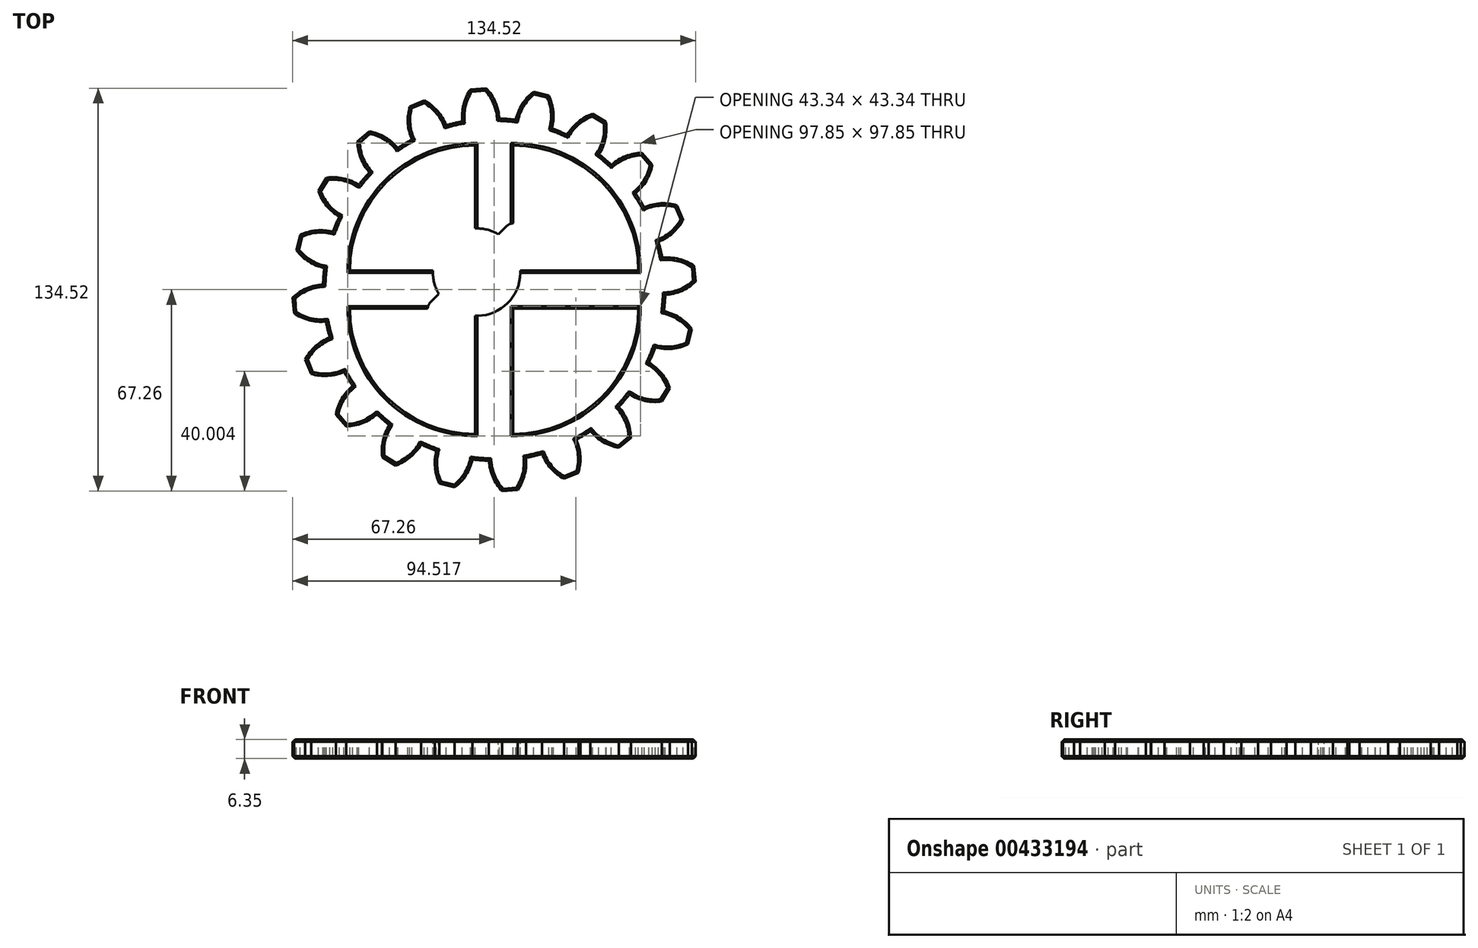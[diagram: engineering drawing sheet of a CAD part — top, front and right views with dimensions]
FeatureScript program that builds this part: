
annotation { "Feature Type Name" : "Feature", "Feature Type Description" : "" }
export const myFeature = defineFeature(function(context is Context, id is Id, definition is map)
    precondition{}
    {
        {
            var Q0;
            Q0=qCreatedBy(makeId("Top.planeOp"),FACE);
            var sketch = newSketch(context, id + "F0", { "sketchPlane" : qUnion([Q0])});
            skCircle(sketch, "E0", {"center": v(0, 0) * mm, "radius": 30.48 * mm, "construction": true});
            skSolve(sketch);
        }
        {
            var Q0;
            Q0=qCreatedBy(makeId("Top.planeOp"),FACE);
            var sketch = newSketch(context, id + "F1", { "sketchPlane" : qUnion([Q0])});
            skCircle(sketch, "E1", {"center": v(0, 0) * mm, "radius": 67.31 * mm, "construction": true});
            skCircle(sketch, "E2", {"center": v(0, 0) * mm, "radius": 63.5 * mm, "construction": true});
            skCircle(sketch, "E3", {"center": v(0, 0) * mm, "radius": 57.15 * mm, "construction": true});
            skLineSegment(sketch, "E4", {"start": v(0, 0) * mm, "end": v(0, 89.78) * mm, "construction": true});
            skLineSegment(sketch, "E5", {"start": v(0, 0) * mm, "end": v(-7.61, 96.72) * mm, "construction": true});
            skLineSegment(sketch, "E6", {"start": v(0, 63.5) * mm, "end": v(-65.71, 63.5) * mm, "construction": true});
            skLineSegment(sketch, "E7", {"start": v(0, 63.5) * mm, "end": v(-58.85, 37.3) * mm, "construction": true});
            skCircle(sketch, "E8", {"center": v(0, 63.5) * mm, "radius": 15.88 * mm, "construction": true});
            skCircle(sketch, "E9", {"center": v(0, 0) * mm, "radius": 58.01 * mm, "construction": true});
            skCircle(sketch, "E10", {"center": v(-14.13, 56.26) * mm, "radius": 15.88 * mm, "construction": true});
            skArc(sketch, "E11", {"start": v(1.72, 57.12) * mm, "mid": v(0.43, 62.59) * mm, "end": v(-2.68, 67.26) * mm});
            skArc(sketch, "E12.MirrorCS", {"start": v(-10.64, 56.15) * mm, "mid": v(-10.22, 61.75) * mm, "end": v(-7.88, 66.85) * mm});
            skLineSegment(sketch, "E13", {"start": v(-7.88, 66.85) * mm, "end": v(-2.68, 67.26) * mm});
            skArc(sketch, "E14", {"start": v(-10.64, 56.15) * mm, "mid": v(4.48, -56.97) * mm, "end": v(1.72, 57.12) * mm});
            skSolve(sketch);
        }
        {
            var Q0;
            Q0=qSketchRegion(id+"F1",true);
            var Q1;
            Q1=makeQuery(id+"Ffi0VH93psu6soF_0.opExtrude","CAP_FACE",FACE,{"disambiguationData":[OSD([sQuery(id+"F0.wireOp",EDGE,"E0")])],"isStart":true});
            extrude(context, id + "F2", {"entities" : qUnion([Q0]), "oppositeDirection" : true, "endBoundEntityFace" : qUnion([Q1]), "depth" : 6.35 * mm});
        }
        {
            var Q0;
            Q0=makeQuery(id+"F2.opExtrude","SWEPT_BODY",BODY,{"disambiguationData":[OSD([sQuery(id+"F1.wireOp",EDGE,"E11"),sQuery(id+"F1.wireOp",EDGE,"E12.MirrorCS"),sQuery(id+"F1.wireOp",EDGE,"E13"),sQuery(id+"F1.wireOp",EDGE,"ZPE7Z8ba-rLlS-d3gG-Tl0h-fifcE816pJjn")])]});
            var Q1;
            Q1=sQuery(id+"F0.wireOp",EDGE,"E0");
            circularPattern(context, id + "F3", {"operationType" : NewBodyOperationType.ADD, "entities" : qUnion([Q0]), "axis" : qUnion([Q1]), "angle" : 360 * degree, "instanceCount" : 20, "equalSpace" : true});
        }
        {
            var Q0;
            {var subQ0=makeQuery(id+"F2.opExtrude","CAP_FACE",FACE,{"disambiguationData":[OSD([sQuery(id+"F1.wireOp",EDGE,"E11"),sQuery(id+"F1.wireOp",EDGE,"E12.MirrorCS"),sQuery(id+"F1.wireOp",EDGE,"E13"),sQuery(id+"F1.wireOp",EDGE,"ZPE7Z8ba-rLlS-d3gG-Tl0h-fifcE816pJjn")])],"isStart":true});Q0=makeQuery(id+"F3.boolean.opBoolean","MERGE",FACE,{"derivedFrom":[makeQuery(id+"Ffi0VH93psu6soF_0.opExtrude","CAP_FACE",FACE,{"disambiguationData":[OSD([sQuery(id+"F0.wireOp",EDGE,"E0")])],"isStart":false}),subQ0,makeQuery(id+"F3.opPattern","COPY",FACE,{"derivedFrom":subQ0,"instanceName":"1"}),makeQuery(id+"F3.opPattern","COPY",FACE,{"derivedFrom":subQ0,"instanceName":"2"}),makeQuery(id+"F3.opPattern","COPY",FACE,{"derivedFrom":subQ0,"instanceName":"3"}),makeQuery(id+"F3.opPattern","COPY",FACE,{"derivedFrom":subQ0,"instanceName":"4"}),makeQuery(id+"F3.opPattern","COPY",FACE,{"derivedFrom":subQ0,"instanceName":"5"}),makeQuery(id+"F3.opPattern","COPY",FACE,{"derivedFrom":subQ0,"instanceName":"6"}),makeQuery(id+"F3.opPattern","COPY",FACE,{"derivedFrom":subQ0,"instanceName":"7"}),makeQuery(id+"F3.opPattern","COPY",FACE,{"derivedFrom":subQ0,"instanceName":"8"}),makeQuery(id+"F3.opPattern","COPY",FACE,{"derivedFrom":subQ0,"instanceName":"9"}),makeQuery(id+"F3.opPattern","COPY",FACE,{"derivedFrom":subQ0,"instanceName":"10"}),makeQuery(id+"F3.opPattern","COPY",FACE,{"derivedFrom":subQ0,"instanceName":"11"}),makeQuery(id+"F3.opPattern","COPY",FACE,{"derivedFrom":subQ0,"instanceName":"12"}),makeQuery(id+"F3.opPattern","COPY",FACE,{"derivedFrom":subQ0,"instanceName":"13"}),makeQuery(id+"F3.opPattern","COPY",FACE,{"derivedFrom":subQ0,"instanceName":"14"})]});}
            var sketch = newSketch(context, id + "F4", { "sketchPlane" : qUnion([Q0])});
            skLineSegment(sketch, "E15", {"start": v(-6.35, 6.35) * mm, "end": v(-48.17, 6.35) * mm});
            skLineSegment(sketch, "E16", {"start": v(-6.35, 6.35) * mm, "end": v(-6.35, 48.17) * mm});
            skArc(sketch, "E17", {"start": v(-6.35, 48.17) * mm, "mid": v(-35.92, 35.92) * mm, "end": v(-48.17, 6.35) * mm});
            skArc(sketch, "E18.1.0", {"start": v(-48.17, -6.35) * mm, "mid": v(-35.92, -35.92) * mm, "end": v(-6.35, -48.17) * mm});
            skLineSegment(sketch, "E18.1.1", {"start": v(-6.35, -6.35) * mm, "end": v(-48.17, -6.35) * mm});
            skLineSegment(sketch, "E18.1.2", {"start": v(-6.35, -6.35) * mm, "end": v(-6.35, -48.17) * mm});
            skArc(sketch, "E18.2.0", {"start": v(6.35, -48.17) * mm, "mid": v(35.92, -35.92) * mm, "end": v(48.17, -6.35) * mm});
            skLineSegment(sketch, "E18.2.1", {"start": v(6.35, -6.35) * mm, "end": v(6.35, -48.17) * mm});
            skLineSegment(sketch, "E18.2.2", {"start": v(6.35, -6.35) * mm, "end": v(48.17, -6.35) * mm});
            skArc(sketch, "E18.3.0", {"start": v(48.17, 6.35) * mm, "mid": v(35.92, 35.92) * mm, "end": v(6.35, 48.17) * mm});
            skLineSegment(sketch, "E18.3.1", {"start": v(6.35, 6.35) * mm, "end": v(48.17, 6.35) * mm});
            skLineSegment(sketch, "E18.3.2", {"start": v(6.35, 6.35) * mm, "end": v(6.35, 48.17) * mm});
            skPoint(sketch, "E18.center", {"position": v(0, 0) * mm});
            skSolve(sketch);
        }
        {
            var Q0;
            Q0=qSketchRegion(id+"F4",true);
            extrude(context, id + "F5", {"entities" : qUnion([Q0]), "operationType" : NewBodyOperationType.REMOVE, "endBound" : BoundingType.THROUGH_ALL, "oppositeDirection" : true, "depth" : 25.4 * mm});
        }
        {
            var Q0;
            {var subQ0=makeQuery(id+"F2.opExtrude","CAP_FACE",FACE,{"disambiguationData":[OSD([sQuery(id+"F1.wireOp",EDGE,"E11"),sQuery(id+"F1.wireOp",EDGE,"E12.MirrorCS"),sQuery(id+"F1.wireOp",EDGE,"E13"),sQuery(id+"F1.wireOp",EDGE,"E14")])],"isStart":true});Q0=makeQuery(id+"F3.boolean.opBoolean","MERGE",FACE,{"derivedFrom":[subQ0,makeQuery(id+"F3.opPattern","COPY",FACE,{"derivedFrom":subQ0,"instanceName":"1"}),makeQuery(id+"F3.opPattern","COPY",FACE,{"derivedFrom":subQ0,"instanceName":"2"}),makeQuery(id+"F3.opPattern","COPY",FACE,{"derivedFrom":subQ0,"instanceName":"3"}),makeQuery(id+"F3.opPattern","COPY",FACE,{"derivedFrom":subQ0,"instanceName":"4"}),makeQuery(id+"F3.opPattern","COPY",FACE,{"derivedFrom":subQ0,"instanceName":"5"}),makeQuery(id+"F3.opPattern","COPY",FACE,{"derivedFrom":subQ0,"instanceName":"6"}),makeQuery(id+"F3.opPattern","COPY",FACE,{"derivedFrom":subQ0,"instanceName":"7"}),makeQuery(id+"F3.opPattern","COPY",FACE,{"derivedFrom":subQ0,"instanceName":"8"}),makeQuery(id+"F3.opPattern","COPY",FACE,{"derivedFrom":subQ0,"instanceName":"9"}),makeQuery(id+"F3.opPattern","COPY",FACE,{"derivedFrom":subQ0,"instanceName":"10"}),makeQuery(id+"F3.opPattern","COPY",FACE,{"derivedFrom":subQ0,"instanceName":"11"}),makeQuery(id+"F3.opPattern","COPY",FACE,{"derivedFrom":subQ0,"instanceName":"12"}),makeQuery(id+"F3.opPattern","COPY",FACE,{"derivedFrom":subQ0,"instanceName":"13"}),makeQuery(id+"F3.opPattern","COPY",FACE,{"derivedFrom":subQ0,"instanceName":"14"}),makeQuery(id+"F3.opPattern","COPY",FACE,{"derivedFrom":subQ0,"instanceName":"15"}),makeQuery(id+"F3.opPattern","COPY",FACE,{"derivedFrom":subQ0,"instanceName":"16"}),makeQuery(id+"F3.opPattern","COPY",FACE,{"derivedFrom":subQ0,"instanceName":"17"}),makeQuery(id+"F3.opPattern","COPY",FACE,{"derivedFrom":subQ0,"instanceName":"18"}),makeQuery(id+"F3.opPattern","COPY",FACE,{"derivedFrom":subQ0,"instanceName":"19"}),makeQuery(id+"F3.opPattern","COPY",FACE,{"derivedFrom":subQ0,"instanceName":"20"}),makeQuery(id+"F3.opPattern","COPY",FACE,{"derivedFrom":subQ0,"instanceName":"21"}),makeQuery(id+"F3.opPattern","COPY",FACE,{"derivedFrom":subQ0,"instanceName":"22"}),makeQuery(id+"F3.opPattern","COPY",FACE,{"derivedFrom":subQ0,"instanceName":"23"})]});}
            var sketch = newSketch(context, id + "F6", { "sketchPlane" : qUnion([Q0])});
            skCircle(sketch, "E19", {"center": v(0, 0) * mm, "radius": 3.18 * mm});
            skSolve(sketch);
        }
        {
            var Q0;
            Q0=qSketchRegion(id+"F6",true);
            extrude(context, id + "F7", {"entities" : qUnion([Q0]), "operationType" : NewBodyOperationType.REMOVE, "oppositeDirection" : true, "depth" : 19.05 * mm});
        }
        {
            var Q0;
            {var subQ0=makeQuery(id+"F2.opExtrude","CAP_FACE",FACE,{"disambiguationData":[OSD([sQuery(id+"F1.wireOp",EDGE,"E11"),sQuery(id+"F1.wireOp",EDGE,"E12.MirrorCS"),sQuery(id+"F1.wireOp",EDGE,"E13"),sQuery(id+"F1.wireOp",EDGE,"E14")])],"isStart":false});Q0=makeQuery(id+"F3.boolean.opBoolean","MERGE",FACE,{"derivedFrom":[subQ0,makeQuery(id+"F3.opPattern","COPY",FACE,{"derivedFrom":subQ0,"instanceName":"1"}),makeQuery(id+"F3.opPattern","COPY",FACE,{"derivedFrom":subQ0,"instanceName":"2"}),makeQuery(id+"F3.opPattern","COPY",FACE,{"derivedFrom":subQ0,"instanceName":"3"}),makeQuery(id+"F3.opPattern","COPY",FACE,{"derivedFrom":subQ0,"instanceName":"4"}),makeQuery(id+"F3.opPattern","COPY",FACE,{"derivedFrom":subQ0,"instanceName":"5"}),makeQuery(id+"F3.opPattern","COPY",FACE,{"derivedFrom":subQ0,"instanceName":"6"}),makeQuery(id+"F3.opPattern","COPY",FACE,{"derivedFrom":subQ0,"instanceName":"7"}),makeQuery(id+"F3.opPattern","COPY",FACE,{"derivedFrom":subQ0,"instanceName":"8"}),makeQuery(id+"F3.opPattern","COPY",FACE,{"derivedFrom":subQ0,"instanceName":"9"}),makeQuery(id+"F3.opPattern","COPY",FACE,{"derivedFrom":subQ0,"instanceName":"10"}),makeQuery(id+"F3.opPattern","COPY",FACE,{"derivedFrom":subQ0,"instanceName":"11"}),makeQuery(id+"F3.opPattern","COPY",FACE,{"derivedFrom":subQ0,"instanceName":"12"}),makeQuery(id+"F3.opPattern","COPY",FACE,{"derivedFrom":subQ0,"instanceName":"13"}),makeQuery(id+"F3.opPattern","COPY",FACE,{"derivedFrom":subQ0,"instanceName":"14"}),makeQuery(id+"F3.opPattern","COPY",FACE,{"derivedFrom":subQ0,"instanceName":"15"}),makeQuery(id+"F3.opPattern","COPY",FACE,{"derivedFrom":subQ0,"instanceName":"16"}),makeQuery(id+"F3.opPattern","COPY",FACE,{"derivedFrom":subQ0,"instanceName":"17"}),makeQuery(id+"F3.opPattern","COPY",FACE,{"derivedFrom":subQ0,"instanceName":"18"}),makeQuery(id+"F3.opPattern","COPY",FACE,{"derivedFrom":subQ0,"instanceName":"19"})]});}
            var Q1;
            {var subQ0=makeQuery(id+"F2.opExtrude","CAP_FACE",FACE,{"disambiguationData":[OSD([sQuery(id+"F1.wireOp",EDGE,"E11"),sQuery(id+"F1.wireOp",EDGE,"E12.MirrorCS"),sQuery(id+"F1.wireOp",EDGE,"E13"),sQuery(id+"F1.wireOp",EDGE,"E14")])],"isStart":true});Q1=makeQuery(id+"F3.boolean.opBoolean","MERGE",FACE,{"derivedFrom":[subQ0,makeQuery(id+"F3.opPattern","COPY",FACE,{"derivedFrom":subQ0,"instanceName":"1"}),makeQuery(id+"F3.opPattern","COPY",FACE,{"derivedFrom":subQ0,"instanceName":"2"}),makeQuery(id+"F3.opPattern","COPY",FACE,{"derivedFrom":subQ0,"instanceName":"3"}),makeQuery(id+"F3.opPattern","COPY",FACE,{"derivedFrom":subQ0,"instanceName":"4"}),makeQuery(id+"F3.opPattern","COPY",FACE,{"derivedFrom":subQ0,"instanceName":"5"}),makeQuery(id+"F3.opPattern","COPY",FACE,{"derivedFrom":subQ0,"instanceName":"6"}),makeQuery(id+"F3.opPattern","COPY",FACE,{"derivedFrom":subQ0,"instanceName":"7"}),makeQuery(id+"F3.opPattern","COPY",FACE,{"derivedFrom":subQ0,"instanceName":"8"}),makeQuery(id+"F3.opPattern","COPY",FACE,{"derivedFrom":subQ0,"instanceName":"9"}),makeQuery(id+"F3.opPattern","COPY",FACE,{"derivedFrom":subQ0,"instanceName":"10"}),makeQuery(id+"F3.opPattern","COPY",FACE,{"derivedFrom":subQ0,"instanceName":"11"}),makeQuery(id+"F3.opPattern","COPY",FACE,{"derivedFrom":subQ0,"instanceName":"12"}),makeQuery(id+"F3.opPattern","COPY",FACE,{"derivedFrom":subQ0,"instanceName":"13"}),makeQuery(id+"F3.opPattern","COPY",FACE,{"derivedFrom":subQ0,"instanceName":"14"}),makeQuery(id+"F3.opPattern","COPY",FACE,{"derivedFrom":subQ0,"instanceName":"15"}),makeQuery(id+"F3.opPattern","COPY",FACE,{"derivedFrom":subQ0,"instanceName":"16"}),makeQuery(id+"F3.opPattern","COPY",FACE,{"derivedFrom":subQ0,"instanceName":"17"}),makeQuery(id+"F3.opPattern","COPY",FACE,{"derivedFrom":subQ0,"instanceName":"18"}),makeQuery(id+"F3.opPattern","COPY",FACE,{"derivedFrom":subQ0,"instanceName":"19"})]});}
            chamfer(context, id + "F8", {"entities" : qUnion([Q0, Q1]), "width" : 0.76 * mm, "tangentPropagation" : true});
        }
        {
            var Q0;
            {var subQ0=makeQuery(id+"F2.opExtrude","CAP_FACE",FACE,{"disambiguationData":[OSD([sQuery(id+"F1.wireOp",EDGE,"E11"),sQuery(id+"F1.wireOp",EDGE,"E12.MirrorCS"),sQuery(id+"F1.wireOp",EDGE,"E13"),sQuery(id+"F1.wireOp",EDGE,"E14")])],"isStart":true});Q0=makeQuery(id+"F3.boolean.opBoolean","MERGE",FACE,{"derivedFrom":[subQ0,makeQuery(id+"F3.opPattern","COPY",FACE,{"derivedFrom":subQ0,"instanceName":"1"}),makeQuery(id+"F3.opPattern","COPY",FACE,{"derivedFrom":subQ0,"instanceName":"2"}),makeQuery(id+"F3.opPattern","COPY",FACE,{"derivedFrom":subQ0,"instanceName":"3"}),makeQuery(id+"F3.opPattern","COPY",FACE,{"derivedFrom":subQ0,"instanceName":"4"}),makeQuery(id+"F3.opPattern","COPY",FACE,{"derivedFrom":subQ0,"instanceName":"5"}),makeQuery(id+"F3.opPattern","COPY",FACE,{"derivedFrom":subQ0,"instanceName":"6"}),makeQuery(id+"F3.opPattern","COPY",FACE,{"derivedFrom":subQ0,"instanceName":"7"}),makeQuery(id+"F3.opPattern","COPY",FACE,{"derivedFrom":subQ0,"instanceName":"8"}),makeQuery(id+"F3.opPattern","COPY",FACE,{"derivedFrom":subQ0,"instanceName":"9"}),makeQuery(id+"F3.opPattern","COPY",FACE,{"derivedFrom":subQ0,"instanceName":"10"}),makeQuery(id+"F3.opPattern","COPY",FACE,{"derivedFrom":subQ0,"instanceName":"11"}),makeQuery(id+"F3.opPattern","COPY",FACE,{"derivedFrom":subQ0,"instanceName":"12"}),makeQuery(id+"F3.opPattern","COPY",FACE,{"derivedFrom":subQ0,"instanceName":"13"}),makeQuery(id+"F3.opPattern","COPY",FACE,{"derivedFrom":subQ0,"instanceName":"14"}),makeQuery(id+"F3.opPattern","COPY",FACE,{"derivedFrom":subQ0,"instanceName":"15"}),makeQuery(id+"F3.opPattern","COPY",FACE,{"derivedFrom":subQ0,"instanceName":"16"}),makeQuery(id+"F3.opPattern","COPY",FACE,{"derivedFrom":subQ0,"instanceName":"17"}),makeQuery(id+"F3.opPattern","COPY",FACE,{"derivedFrom":subQ0,"instanceName":"18"}),makeQuery(id+"F3.opPattern","COPY",FACE,{"derivedFrom":subQ0,"instanceName":"19"})]});}
            var sketch = newSketch(context, id + "F9", { "sketchPlane" : qUnion([Q0])});
            skCircle(sketch, "E20", {"center": v(-5.84, 5.84) * mm, "radius": 14.6 * mm});
            skLineSegment(sketch, "E21", {"start": v(0, 0) * mm, "end": v(-5.59, 5.59) * mm, "construction": true});
            skSolve(sketch);
        }
        {
            var Q0;
            Q0 = qSketchRegion(id + "F9", true);
            extrude(context, id + "F10", {"entities" : qUnion([Q0]), "operationType" : NewBodyOperationType.REMOVE, "endBound" : BoundingType.THROUGH_ALL, "oppositeDirection" : true, "depth" : 25.4 * mm, "offsetDistance" : 25.4 * mm});
        }
        {
            var Q0;
            {var subQ0=makeQuery(id+"F2.opExtrude","CAP_FACE",FACE,{"disambiguationData":[OSD([sQuery(id+"F1.wireOp",EDGE,"E11"),sQuery(id+"F1.wireOp",EDGE,"E12.MirrorCS"),sQuery(id+"F1.wireOp",EDGE,"E13"),sQuery(id+"F1.wireOp",EDGE,"E14")])],"isStart":true});Q0=makeQuery(id+"F3.boolean.opBoolean","MERGE",FACE,{"derivedFrom":[subQ0,makeQuery(id+"F3.opPattern","COPY",FACE,{"derivedFrom":subQ0,"instanceName":"1"}),makeQuery(id+"F3.opPattern","COPY",FACE,{"derivedFrom":subQ0,"instanceName":"2"}),makeQuery(id+"F3.opPattern","COPY",FACE,{"derivedFrom":subQ0,"instanceName":"3"}),makeQuery(id+"F3.opPattern","COPY",FACE,{"derivedFrom":subQ0,"instanceName":"4"}),makeQuery(id+"F3.opPattern","COPY",FACE,{"derivedFrom":subQ0,"instanceName":"5"}),makeQuery(id+"F3.opPattern","COPY",FACE,{"derivedFrom":subQ0,"instanceName":"6"}),makeQuery(id+"F3.opPattern","COPY",FACE,{"derivedFrom":subQ0,"instanceName":"7"}),makeQuery(id+"F3.opPattern","COPY",FACE,{"derivedFrom":subQ0,"instanceName":"8"}),makeQuery(id+"F3.opPattern","COPY",FACE,{"derivedFrom":subQ0,"instanceName":"9"}),makeQuery(id+"F3.opPattern","COPY",FACE,{"derivedFrom":subQ0,"instanceName":"10"}),makeQuery(id+"F3.opPattern","COPY",FACE,{"derivedFrom":subQ0,"instanceName":"11"}),makeQuery(id+"F3.opPattern","COPY",FACE,{"derivedFrom":subQ0,"instanceName":"12"}),makeQuery(id+"F3.opPattern","COPY",FACE,{"derivedFrom":subQ0,"instanceName":"13"}),makeQuery(id+"F3.opPattern","COPY",FACE,{"derivedFrom":subQ0,"instanceName":"14"}),makeQuery(id+"F3.opPattern","COPY",FACE,{"derivedFrom":subQ0,"instanceName":"15"}),makeQuery(id+"F3.opPattern","COPY",FACE,{"derivedFrom":subQ0,"instanceName":"16"}),makeQuery(id+"F3.opPattern","COPY",FACE,{"derivedFrom":subQ0,"instanceName":"17"}),makeQuery(id+"F3.opPattern","COPY",FACE,{"derivedFrom":subQ0,"instanceName":"18"}),makeQuery(id+"F3.opPattern","COPY",FACE,{"derivedFrom":subQ0,"instanceName":"19"})]});}
            var sketch = newSketch(context, id + "F11", { "sketchPlane" : qUnion([Q0])});
            skLineSegment(sketch, "E22", {"start": v(9.43, 15.72) * mm, "end": v(-15.72, -9.43) * mm});
            skLineSegment(sketch, "E23", {"start": v(4.04, 21.1) * mm, "end": v(-21.1, -4.04) * mm});
            skArc(sketch, "E24", {"start": v(9.43, 15.72) * mm, "mid": v(9.43, 21.1) * mm, "end": v(4.04, 21.1) * mm});
            skArc(sketch, "E25", {"start": v(-21.1, -4.04) * mm, "mid": v(-21.1, -9.43) * mm, "end": v(-15.72, -9.43) * mm});
            skLineSegment(sketch, "E26", {"start": v(6.74, 18.4) * mm, "end": v(-18.4, -6.74) * mm, "construction": true});
            skPoint(sketch, "E27", {"position": v(9.43, 21.1) * mm});
            skPoint(sketch, "E28", {"position": v(-21.1, -9.43) * mm});
            skPoint(sketch, "E29", {"position": v(-5.84, 5.84) * mm});
            skLineSegment(sketch, "E30", {"start": v(0, 0) * mm, "end": v(-5.84, 5.84) * mm, "construction": true});
            skSolve(sketch);
        }
        {
            var Q0;
            Q0 = qSketchRegion(id + "F11", true);
            extrude(context, id + "F12", {"entities" : qUnion([Q0]), "operationType" : NewBodyOperationType.REMOVE, "endBound" : BoundingType.THROUGH_ALL, "oppositeDirection" : true, "depth" : 25.4 * mm, "offsetDistance" : 25.4 * mm});
        }
    });
